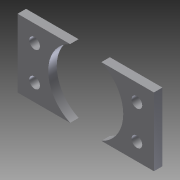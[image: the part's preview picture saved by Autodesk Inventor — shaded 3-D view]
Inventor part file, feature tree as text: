
AUTODESK INVENTOR PART (.ipt)
format: ipt  version: 2011 (Build 150239000, 239)  size: 93,696 bytes
history: native  units: in
note: dims shown in document units (in); Inventor stores cm internally (conversion verified against a paired STEP export)
features: sketch x3, extrude x2, hole x1
ambient origin geometry x8: Origin, YZ Plane, XZ Plane, XY Plane, X Axis, Y Axis, Z Axis, Center Point
bodies: Solid1 (feature_tree)
feature tree (6):
  extrude  "Extrusion1"  Depth=0.5in
  extrude  "Extrusion2"  Depth=0.55in
  hole  "Hole3"  [1 undecoded]
  sketch  "Sketch1"  dims[d0=1.0in d1=0.5in]
  sketch  "Sketch2"  dims[d2=0.0625in d3=0.0in d4=0.55in]
  sketch  "Sketch6"  dims[d5=0.0625in d6=0.0in d21=0.0787in d22=0.75in d23=0.375in d24=0.25in d25=0.5635in d26=1.0in d27=0.8108in]
note: 1 required parameter value undecoded (feature->parameter linkage not recoverable at this tier; creation-order binding heuristic only, values carry confidence <= 0.55)
